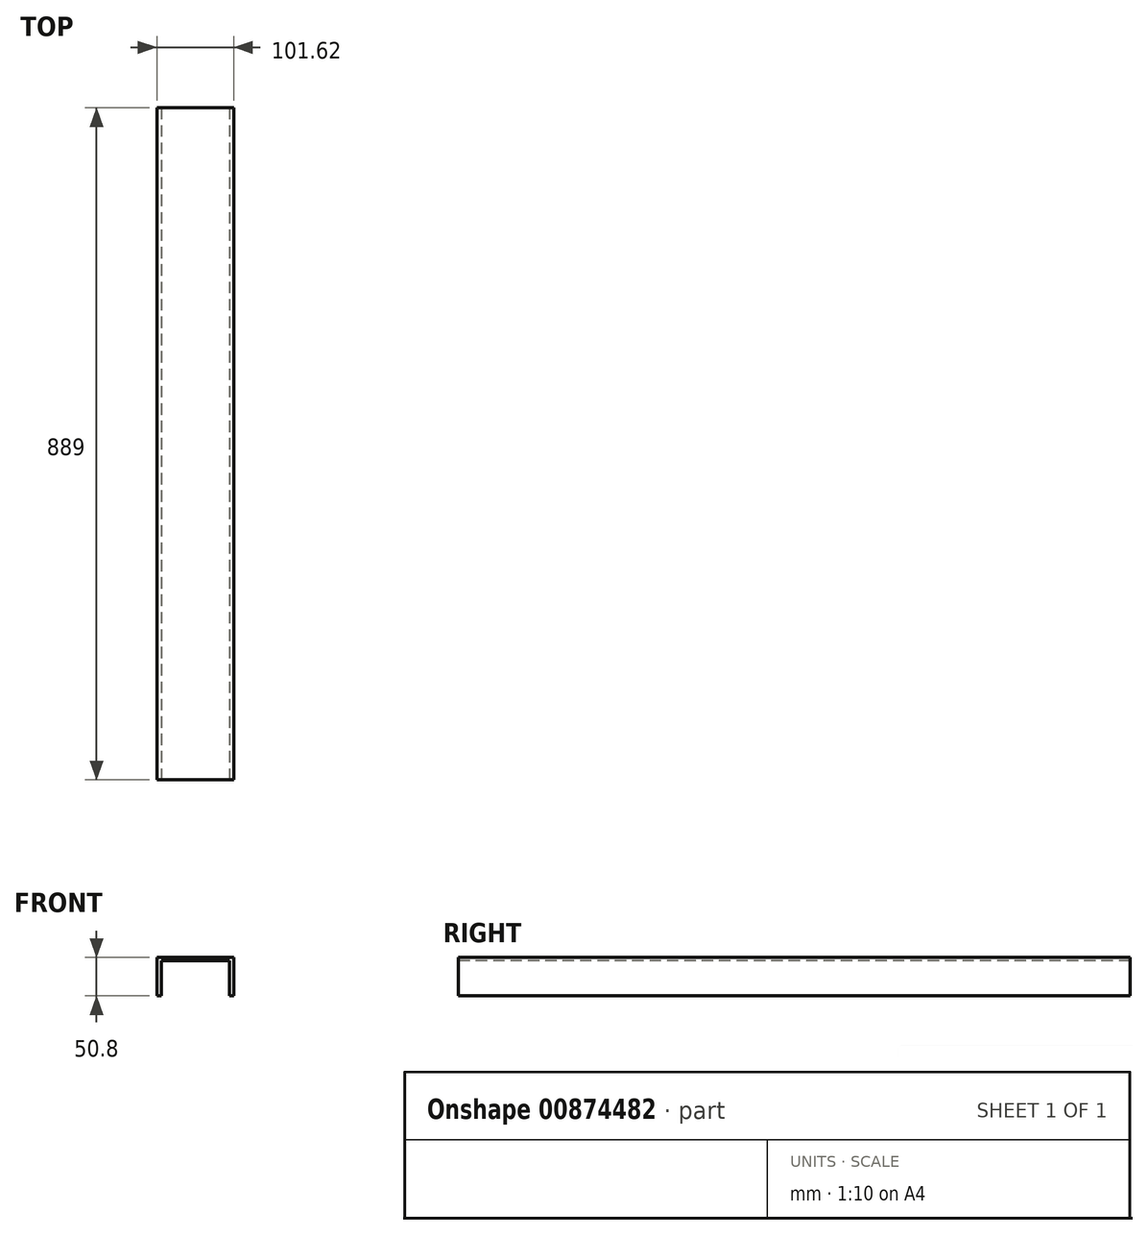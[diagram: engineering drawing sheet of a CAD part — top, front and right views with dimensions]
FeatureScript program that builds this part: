
annotation { "Feature Type Name" : "Feature", "Feature Type Description" : "" }
export const myFeature = defineFeature(function(context is Context, id is Id, definition is map)
    precondition{}
    {
        {
            var Q0;
            Q0=qCreatedBy(makeId("Front.planeOp"),FACE);
            var sketch = newSketch(context, id + "F0", { "sketchPlane" : qUnion([Q0])});
            skLineSegment(sketch, "E0.bottom", {"start": v(-50.79, 25.4) * mm, "end": v(50.81, 25.4) * mm});
            skLineSegment(sketch, "E0.left", {"start": v(-50.79, 25.4) * mm, "end": v(-50.81, -25.4) * mm});
            skLineSegment(sketch, "E0.right", {"start": v(50.81, 25.4) * mm, "end": v(50.79, -25.4) * mm});
            skPoint(sketch, "E0.middle", {"position": v(0, 0) * mm});
            skLineSegment(sketch, "E1", {"start": v(-45.27, -25.4) * mm, "end": v(-45.27, 21.13) * mm});
            skLineSegment(sketch, "E2", {"start": v(-45.27, 21.13) * mm, "end": v(45.25, 21.13) * mm});
            skLineSegment(sketch, "E3", {"start": v(45.25, 21.13) * mm, "end": v(45.25, -25.4) * mm});
            skLineSegment(sketch, "E4", {"start": v(-50.81, -25.4) * mm, "end": v(-45.27, -25.4) * mm});
            skLineSegment(sketch, "E5", {"start": v(45.25, -25.4) * mm, "end": v(50.79, -25.4) * mm});
            skSolve(sketch);
        }
        {
            var Q0;
            Q0 = qSketchRegion(id + "F0", true);
            extrude(context, id + "F1", {"entities" : qUnion([Q0]), "oppositeDirection" : true, "depth" : 889 * mm, "offsetDistance" : 25.4 * mm});
        }
    });
